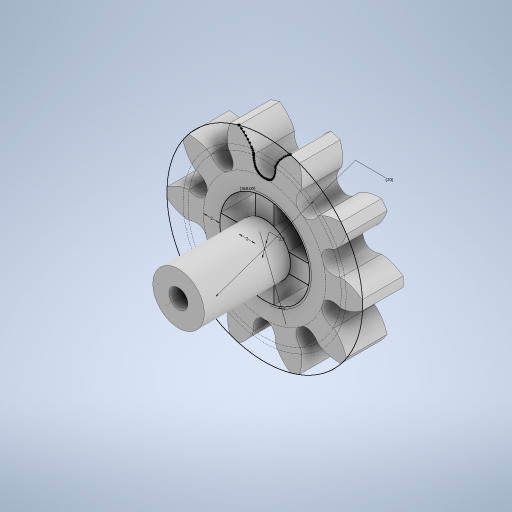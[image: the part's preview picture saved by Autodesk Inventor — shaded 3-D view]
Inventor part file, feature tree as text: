
AUTODESK INVENTOR PART (.ipt)
format: ipt  version: 2023 (Build 270158000, 158)  size: 412,160 bytes
history: native  units: mm
features: extrude x4, sketch x1, pattern_circular x1
ambient origin geometry x8: Origin, YZ Plane, XZ Plane, XY Plane, X Axis, Y Axis, Z Axis, Center Point
bodies: Solid1 (feature_tree)
feature tree (6):
  sketch  "Sketch1"  dims[d0=5.0mm d1=0.0mm d2=2.3mm d3=2.0mm d4=2.0mm d5=40.0mm d7=360.0deg d9=0.0mm d10=0.0mm d11=100.0mm d12=360.0deg d14=0.0mm d15=0.0mm d16=10.56mm d17=0.0mm d18=20.0mm]
  extrude  "Extrusion1"  TaperAngle=0.0deg  [1 undecoded]
  extrude  "Extrusion2"  Depth=2.3mm
  pattern_circular  "Circular Pattern1"  [2 undecoded]
  extrude  "Extrusion3"  Depth=10.56mm
  extrude  "Extrusion4"  Depth=10.56mm TaperAngle=360.0deg
note: 3 required parameter values undecoded (feature->parameter linkage not recoverable at this tier; creation-order binding heuristic only, values carry confidence <= 0.55)
